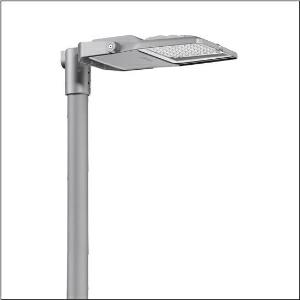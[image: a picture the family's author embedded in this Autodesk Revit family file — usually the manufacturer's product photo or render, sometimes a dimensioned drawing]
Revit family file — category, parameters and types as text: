
# Revit family: floodlight_fl_21_iq_mini___pl61_5xa7771b4c3a_e6c4
name_source: partatom
category: Lighting Fixtures
units: mm (PartAtom-declared; Revit-internal decimal feet)

## family parameters
Cut with Voids When Loaded = No
Host = Face
Light Source = No
Part Type = Normal
Room Calculation Point = No
Round Connector Dimension = Use Diameter
Shared = No

## types (1)
- --- (1 x LED, 6370 lm, 45.5 W, 4000K)
    Apparent Load = 46 VA
    CIE Flux Codes = 33 65 98 100 100
    Color Rendering = 70
    Color Temperature = 4000K
    Default Elevation = 1800 mm
    Description = Floodlight FL 21 iQ mini, floodlight, primary light control with lens, of PMMA, primary optical cover: protective disc, of toughened safety glass, transparent, light distribution: PL61, light emission: direct distribution, installation type: surface-mounted, LED, High Power LED, rated luminous flux: 6.370lm, luminous efficacy: 140lm/W, light colour: 740, colour temperature: 4000K, control: Auto-Match, Temp-Guard, Lumen-Switch, Night-Set, Smart-Wire, Light-Fading, Desk-Remote (wireless, voltage-free reading and setting of iQ features in the workshop via application-optimized NFC function/RFID function), optimised constant luminous flux control (CLO 2.0), with terminal, 6-pole, mains connection: 220..240V, AC, 50/60Hz, start of lifetime: 46W, end of service life: 48W, reduction: 22W, luminaire housing, of diecast aluminium, powder-coated, Siteco® metallic grey (DB 702S), corrosivity category C5 mid according to DIN EN ISO 12944, sealing non-destructively replaceable, please order mast flange separately, mast bracket, of steel, galvanised, powder-coated, Siteco® metallic grey (DB 702S), protection rating (complete): IP66, insulation class (complete): insulation class II (safety insulation), certification: CE, ENEC, VDE, protection symbol: D, impact resistance: IK08, permissible operating ambient temperature: -40..+40°C, permissible operating ambient temperature for outdoor applications: -40..+50°C, standard: DIN EN 12944, LABS conformity tested according to VDMA 24364:2018-05, packaging unit: 1 piece

Light Distribution: PL61
    Height = 70 mm
    Lamp = 1 x LED
    Lamp Light Flux = 6370 lm
    Lamp Power = 45.5 W
    Lamp count = 1
    Length = 485 mm
    Luminous efficacy = 140 lm/W
    Manufacturer = Siteco
    ModVariant = No
    Model = 5XA7771B4C3A
    Number of Poles = 1
    OnlyDefault = Yes
    Power Factor = 1
    Product Name = Floodlight FL 21 iQ mini | PL61
    Product group = floodlight | pylon annexe
    ProductGroupID = 6200
    Protection Class = Protection class II
    Protection Degree = IP 66
    RLX_Detail_Level = 1
    RLX_Emergency_Light_Flux = 0 lm
    RLX_Emergency_Type = 0
    RLX_Emergency_Type_DB = No
    RlxData = <blob elided: 101325 chars, md5=5b94588f>
    Socket = socket
    Standby Power = 0 W
    System Light Flux = 6370 lm
    System Power = 46 W
    Type Comments = factory setting: luminous flux: 100 % | dim-lin: 254 | 463 mA
    Type Image = l_1007125.jpg
    URL = http://relux.com
    VarID = @adj_144837
    Voltage = 0 V
    Weight = 0.00 kg
    Width = 337 mm

## geometry (parser evidence)
native form markers: Blend x4, Sweep x13
no freeform markers — native parametric forms only
